# Revit family: Planter-Elevated-CityScapes-Planx
name_source: partatom
category: Specialty Equipment
units: mm (PartAtom-declared; Revit-internal decimal feet)

## family parameters
Always vertical = Yes
Cut with Voids When Loaded = No
Part Type = Normal
Room Calculation Point = No
Round Connector Dimension = Use Diameter
Shared = No
Work Plane-Based = No

## types (5) — shared parameters
CAD Details = https://www.arcat.com
Default Elevation = 0"
Description = Elevated Planter
Height = 34"
Keynote = 32 94 33
Manufacturer = CityScapes
Model = Planx Planters - Elevated Planters Series
Product Page URL = https://www.arcat.com
Specification = https://www.arcat.com
URL = https://cityscapesinc.com

## per-type parameters (varying)
| type | Leg Visibility | Length | Width |
| 18”x48”x34” | No | 24" | 60" |
| 24”x48”x34” | No | 24" | 48" |
| 24”x72”x34” | Yes | 24" | 72" |
| 24”x60”x34” | No | 24" | 60" |
| 18”x36”x34” | No | 18" | 36" |

## geometry (parser evidence)
native form markers: Sweep x3
no freeform markers — native parametric forms only
